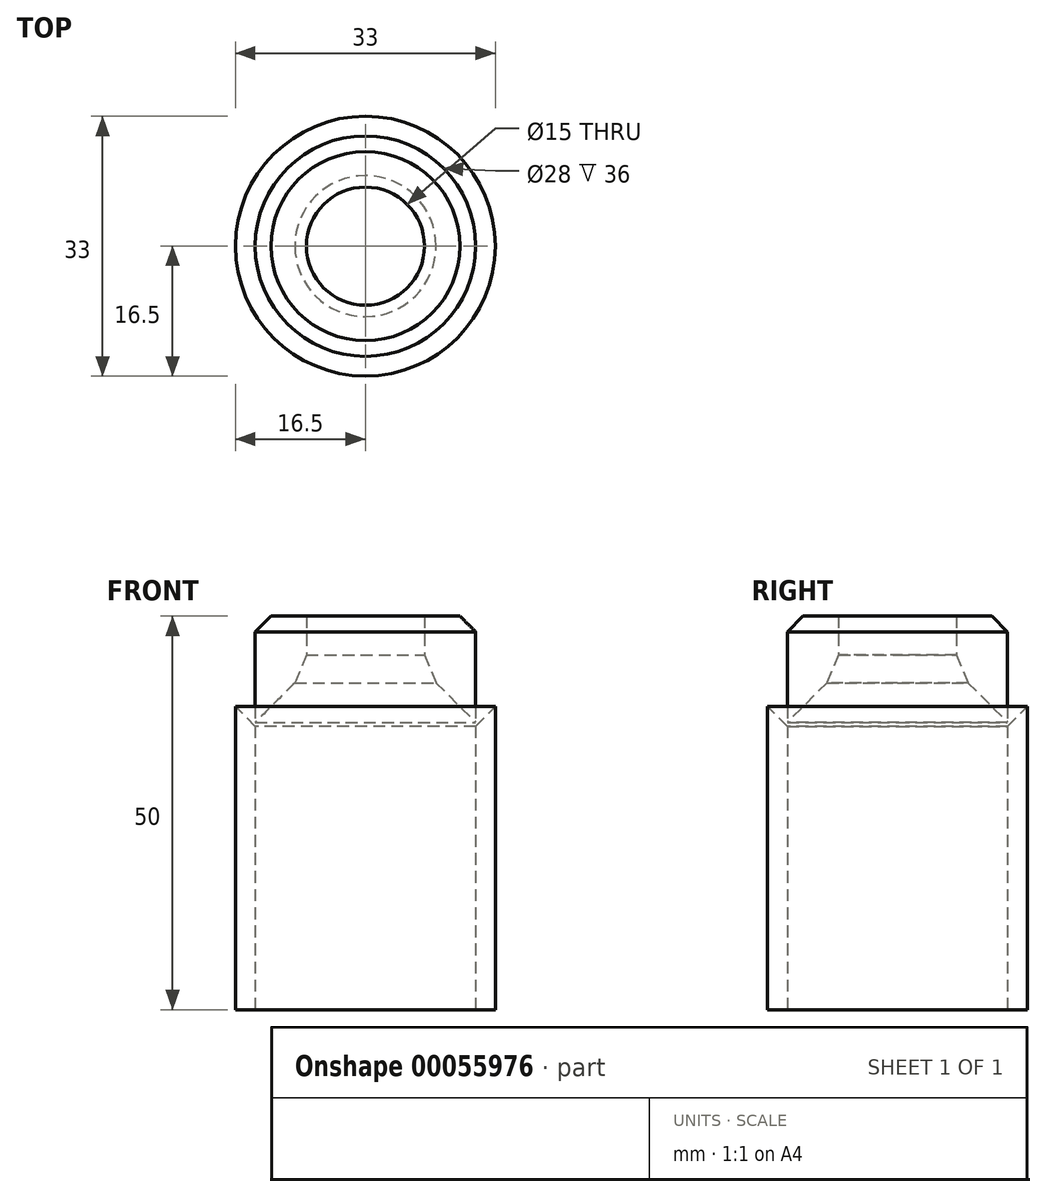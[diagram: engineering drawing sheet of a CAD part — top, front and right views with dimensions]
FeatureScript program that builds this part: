
annotation { "Feature Type Name" : "Feature", "Feature Type Description" : "" }
export const myFeature = defineFeature(function(context is Context, id is Id, definition is map)
    precondition{}
    {
        {
            var Q0;
            Q0=qCreatedBy(makeId("Top.planeOp"),FACE);
            var sketch = newSketch(context, id + "F0", { "sketchPlane" : qUnion([Q0])});
            skCircle(sketch, "E0", {"center": v(0, 0) * mm, "radius": 16.5 * mm});
            skCircle(sketch, "E1", {"center": v(0, 0) * mm, "radius": 14 * mm});
            skSolve(sketch);
        }
        {
            var Q0;
            Q0=makeQuery(id+"F0.imprint","IMPRINT",FACE,{"disambiguationData":[TD([[makeQuery(id+"F0.imprint","IMPRINT",EDGE,{"derivedFrom":sQuery(id+"F0.wireOp",EDGE,"E0")}),1.0]])]});
            extrude(context, id + "F1", {"entities" : qUnion([Q0]), "depth" : 40 * mm});
        }
        {
            var Q0;
            Q0=makeQuery(id+"F1.opExtrude","CAP_FACE",FACE,{"disambiguationData":[OSD([sQuery(id+"F0.wireOp",EDGE,"E0"),sQuery(id+"F0.wireOp",EDGE,"E1")])],"isStart":false});
            var sketch = newSketch(context, id + "F2", { "sketchPlane" : qUnion([Q0])});
            skCircle(sketch, "E2", {"center": v(0, 0) * mm, "radius": 7.5 * mm});
            skSolve(sketch);
        }
        {
            var Q0;
            Q0=makeQuery(id+"F2.imprint","IMPRINT",FACE,{"disambiguationData":[TD([[makeQuery(id+"F2.imprint","IMPRINT",EDGE,{"derivedFrom":sQuery(id+"F2.wireOp",EDGE,"E2")}),-1.0]])]});
            extrude(context, id + "F3", {"entities" : qUnion([Q0]), "depth" : 10 * mm, "hasSecondDirection" : true, "secondDirectionOppositeDirection" : true, "secondDirectionDepth" : 5 * mm});
        }
        {
            var Q0;
            Q0=makeQuery(id+"F1.opExtrude","CAP_EDGE",EDGE,{"disambiguationData":[OSD([sQuery(id+"F0.wireOp",EDGE,"E1")])],"isStart":false});
            chamfer(context, id + "F4", {"entities" : qUnion([Q0]), "width" : 4 * mm, "tangentPropagation" : true});
        }
        {
            var Q0;
            Q0=makeQuery(id+"F3.opExtrude","CAP_EDGE",EDGE,{"disambiguationData":[OSD([sQuery(id+"F0.wireOp",EDGE,"E1")])],"isStart":false});
            chamfer(context, id + "F5", {"entities" : qUnion([Q0]), "width" : 2 * mm, "tangentPropagation" : true});
        }
        {
            var Q0;
            Q0=makeQuery(id+"F3.opExtrude","CAP_EDGE",EDGE,{"disambiguationData":[OSD([sQuery(id+"F2.wireOp",EDGE,"E2")])],"isStart":true});
            chamfer(context, id + "F6", {"entities" : qUnion([Q0]), "width" : 8 * mm, "tangentPropagation" : true});
        }
        {
            var Q0;
            {var subQ0=sQuery(id+"F2.wireOp",EDGE,"E2");Q0=makeQuery(id+"F6.opChamfer","BLEND_EDGE",EDGE,{"blendedFrom":[makeQuery(id+"F3.opExtrude","CAP_EDGE",EDGE,{"disambiguationData":[OSD([subQ0])],"isStart":true}),makeQuery(id+"F3.opExtrude","SWEPT_FACE",FACE,{"disambiguationData":[OSD([subQ0])]})],"blendedInto":[makeQuery(id+"F3.opExtrude","SWEPT_FACE",FACE,{"disambiguationData":[OSD([subQ0])]})]});}
            chamfer(context, id + "F7", {"entities" : qUnion([Q0]), "width" : 5 * mm, "tangentPropagation" : true});
        }
    });
